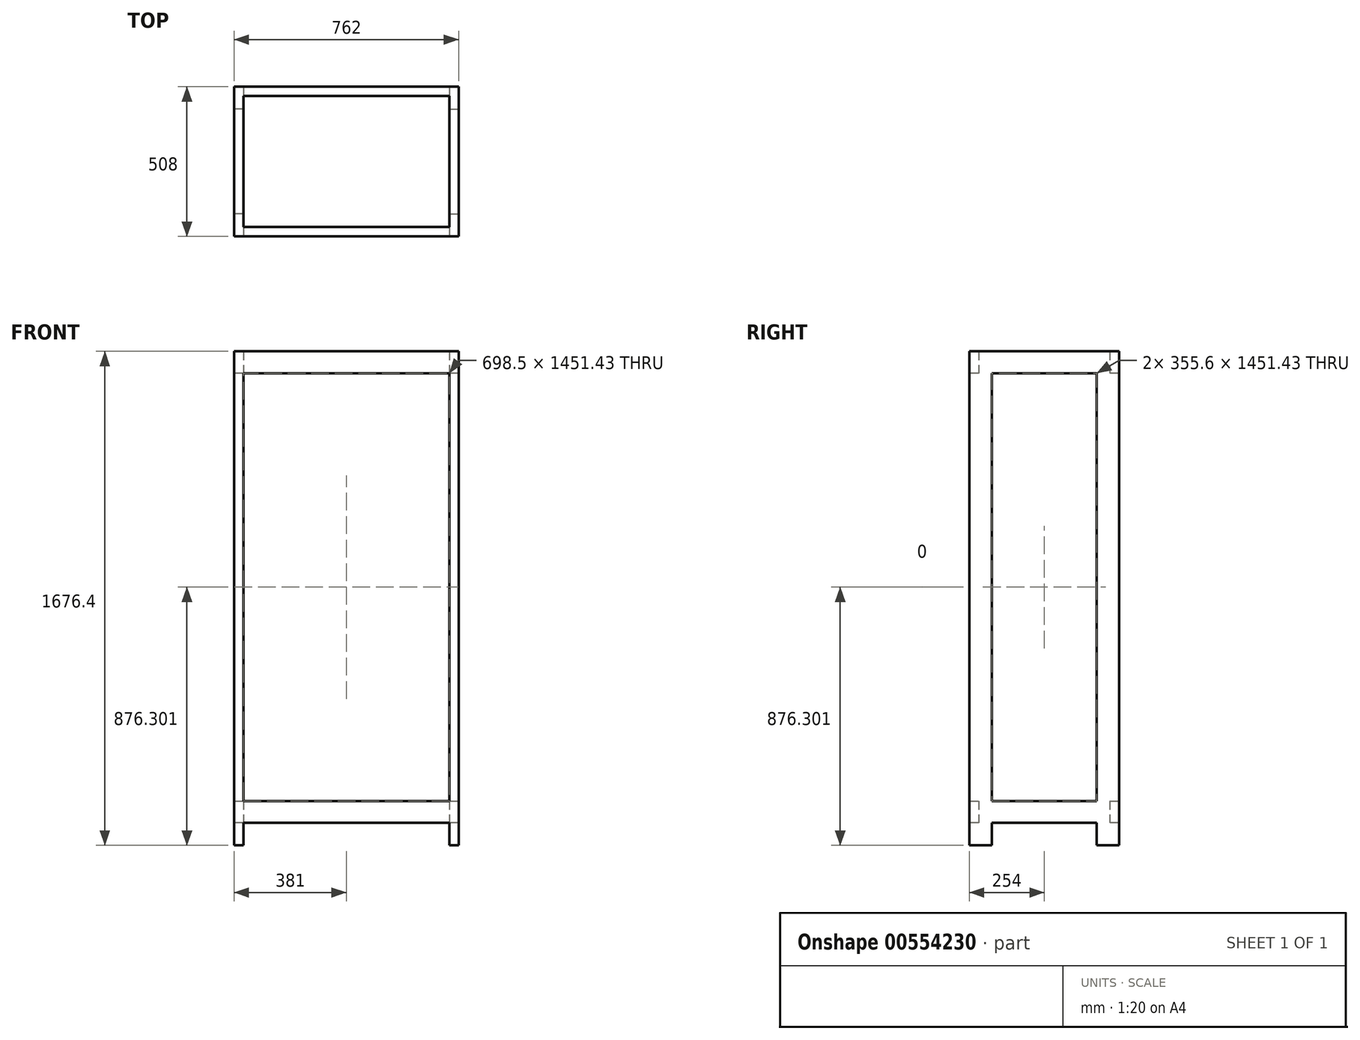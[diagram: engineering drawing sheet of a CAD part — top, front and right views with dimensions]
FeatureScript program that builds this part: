
annotation { "Feature Type Name" : "Feature", "Feature Type Description" : "" }
export const myFeature = defineFeature(function(context is Context, id is Id, definition is map)
    precondition{}
    {
        {
            var Q0;
            Q0=qCreatedBy(makeId("Front.planeOp"),FACE);
            var sketch = newSketch(context, id + "F0", { "sketchPlane" : qUnion([Q0])});
            skLineSegment(sketch, "E0.bottom", {"start": v(381, 1497.94) * mm, "end": v(349.25, 1497.94) * mm});
            skLineSegment(sketch, "E0.top", {"start": v(381, -178.46) * mm, "end": v(349.25, -178.46) * mm});
            skLineSegment(sketch, "E0.left", {"start": v(381, 1497.94) * mm, "end": v(381, -178.46) * mm});
            skLineSegment(sketch, "E0.right", {"start": v(349.25, 1497.94) * mm, "end": v(349.25, -178.46) * mm});
            skLineSegment(sketch, "E1", {"start": v(0, 72.38) * mm, "end": v(0, -157.13) * mm, "construction": true});
            skLineSegment(sketch, "E2.MirrorCS", {"start": v(-381, 1497.94) * mm, "end": v(-381, -178.46) * mm});
            skLineSegment(sketch, "E3.MirrorCS", {"start": v(-349.25, 1497.94) * mm, "end": v(-349.25, -178.46) * mm});
            skLineSegment(sketch, "E4.MirrorCS", {"start": v(-381, -178.46) * mm, "end": v(-349.25, -178.46) * mm});
            skLineSegment(sketch, "E5.MirrorCS", {"start": v(-381, 1497.94) * mm, "end": v(-349.25, 1497.94) * mm});
            skLineSegment(sketch, "E6", {"start": v(-349.25, 1497.94) * mm, "end": v(-349.25, 1423.55) * mm});
            skLineSegment(sketch, "E7", {"start": v(-349.25, 1423.55) * mm, "end": v(349.25, 1423.55) * mm});
            skLineSegment(sketch, "E8", {"start": v(349.25, 1423.55) * mm, "end": v(349.25, 1497.94) * mm});
            skLineSegment(sketch, "E9", {"start": v(-349.25, 1497.94) * mm, "end": v(349.25, 1497.94) * mm});
            skLineSegment(sketch, "E10", {"start": v(349.25, 697.84) * mm, "end": v(-349.25, 697.84) * mm, "construction": true});
            skLineSegment(sketch, "E11.MirrorCS", {"start": v(-349.25, -102.26) * mm, "end": v(349.25, -102.26) * mm});
            skLineSegment(sketch, "E12.MirrorCS", {"start": v(-349.25, -27.87) * mm, "end": v(349.25, -27.87) * mm});
            skLineSegment(sketch, "E13.MirrorCS", {"start": v(349.25, -27.87) * mm, "end": v(349.25, -102.26) * mm});
            skLineSegment(sketch, "E14.MirrorCS", {"start": v(-349.25, -102.26) * mm, "end": v(-349.25, -27.87) * mm});
            skLineSegment(sketch, "E15", {"start": v(-349.25, -65.07) * mm, "end": v(-365.12, -65.07) * mm});
            skLineSegment(sketch, "E16", {"start": v(-365.12, -65.07) * mm, "end": v(-365.13, 1460.75) * mm});
            skPoint(sketch, "E16.endSnap0", {"position": v(-349.25, 1460.75) * mm});
            skLineSegment(sketch, "E17", {"start": v(-365.13, 1460.75) * mm, "end": v(-349.25, 1460.75) * mm});
            skLineSegment(sketch, "E18", {"start": v(0, 1460.75) * mm, "end": v(-349.25, 1460.75) * mm});
            skLineSegment(sketch, "E19", {"start": v(0, -65.07) * mm, "end": v(-349.25, -65.07) * mm});
            skLineSegment(sketch, "E20.MirrorCS", {"start": v(0, -65.07) * mm, "end": v(349.25, -65.07) * mm});
            skLineSegment(sketch, "E21.MirrorCS", {"start": v(365.12, -65.07) * mm, "end": v(365.12, 1460.75) * mm});
            skLineSegment(sketch, "E22.MirrorCS", {"start": v(349.25, -65.07) * mm, "end": v(365.13, -65.07) * mm});
            skLineSegment(sketch, "E23.MirrorCS", {"start": v(365.12, 1460.75) * mm, "end": v(349.25, 1460.75) * mm});
            skLineSegment(sketch, "E24.MirrorCS", {"start": v(0, 1460.75) * mm, "end": v(349.25, 1460.75) * mm});
            skLineSegment(sketch, "E25", {"start": v(-349.25, 1423.55) * mm, "end": v(-381, 1423.55) * mm});
            skLineSegment(sketch, "E26", {"start": v(-349.25, -102.26) * mm, "end": v(-381, -102.26) * mm});
            skLineSegment(sketch, "E27", {"start": v(-381, -102.26) * mm, "end": v(-381, -27.87) * mm});
            skLineSegment(sketch, "E28", {"start": v(-381, -27.87) * mm, "end": v(-349.25, -27.87) * mm});
            skLineSegment(sketch, "E29.MirrorCS", {"start": v(349.25, -102.26) * mm, "end": v(381, -102.26) * mm});
            skLineSegment(sketch, "E30.MirrorCS", {"start": v(381, -27.87) * mm, "end": v(349.25, -27.87) * mm});
            skLineSegment(sketch, "E31.MirrorCS", {"start": v(381, -102.26) * mm, "end": v(381, -27.87) * mm});
            skLineSegment(sketch, "E32.MirrorCS", {"start": v(349.25, 1423.55) * mm, "end": v(381, 1423.55) * mm});
            skLineSegment(sketch, "E33.0", {"start": v(-349.25, -39.67) * mm, "end": v(-365.12, -39.67) * mm});
            skLineSegment(sketch, "E33.1", {"start": v(0, -39.67) * mm, "end": v(-349.25, -39.67) * mm});
            skLineSegment(sketch, "E33.2", {"start": v(0, -39.67) * mm, "end": v(349.25, -39.67) * mm});
            skLineSegment(sketch, "E33.3", {"start": v(349.25, -39.67) * mm, "end": v(365.13, -39.67) * mm});
            skLineSegment(sketch, "E34.0", {"start": v(365.12, 1435.35) * mm, "end": v(349.25, 1435.35) * mm});
            skLineSegment(sketch, "E34.1", {"start": v(0, 1435.35) * mm, "end": v(349.25, 1435.35) * mm});
            skLineSegment(sketch, "E34.2", {"start": v(0, 1435.35) * mm, "end": v(-349.25, 1435.35) * mm});
            skLineSegment(sketch, "E34.3", {"start": v(-365.13, 1435.35) * mm, "end": v(-349.25, 1435.35) * mm});
            skSolve(sketch);
        }
        {
            var Q0;
            {var subQ3=sQuery(id+"F0.wireOp",EDGE,"E23.MirrorCS");Q0=makeQuery(id+"F0.imprint","IMPRINT",FACE,{"disambiguationData":[TD([[makeQuery(id+"F0.imprint","IMPRINT",EDGE,{"derivedFrom":subQ3}),1.0]])]});}
            var Q1;
            {var subQ5=sQuery(id+"F0.wireOp",EDGE,"E0.bottom");Q1=makeQuery(id+"F0.imprint","IMPRINT",FACE,{"disambiguationData":[TD([[makeQuery(id+"F0.imprint","IMPRINT",EDGE,{"derivedFrom":subQ5}),1.0]])]});}
            var Q2;
            {var subQ0=sQuery(id+"F0.wireOp",EDGE,"E30.MirrorCS");var subQ5=sQuery(id+"F0.wireOp",EDGE,"E21.MirrorCS");var subQ6=makeQuery(id+"F0.imprint","INTERSECT",VERTEX,{"derivedFrom":[subQ5,subQ0]});Q2=makeQuery(id+"F0.imprint","IMPRINT",FACE,{"disambiguationData":[TD([[makeQuery(id+"F0.imprint","IMPRINT",EDGE,{"disambiguationData":[TD([[subQ6,-1.0]])],"derivedFrom":subQ5}),-1.0]])]});}
            var Q3;
            {var subQ3=sQuery(id+"F0.wireOp",EDGE,"E30.MirrorCS");var subQ5=sQuery(id+"F0.wireOp",EDGE,"E21.MirrorCS");var subQ6=makeQuery(id+"F0.imprint","INTERSECT",VERTEX,{"derivedFrom":[subQ5,subQ3]});Q3=makeQuery(id+"F0.imprint","IMPRINT",FACE,{"disambiguationData":[TD([[makeQuery(id+"F0.imprint","IMPRINT",EDGE,{"disambiguationData":[TD([[subQ6,-1.0]])],"derivedFrom":subQ5}),1.0]])]});}
            var Q4;
            {var subQ1=sQuery(id+"F0.wireOp",EDGE,"E22.MirrorCS");Q4=makeQuery(id+"F0.imprint","IMPRINT",FACE,{"disambiguationData":[TD([[makeQuery(id+"F0.imprint","IMPRINT",EDGE,{"derivedFrom":subQ1}),-1.0]])]});}
            var Q5;
            {var subQ3=sQuery(id+"F0.wireOp",EDGE,"E22.MirrorCS");Q5=makeQuery(id+"F0.imprint","IMPRINT",FACE,{"disambiguationData":[TD([[makeQuery(id+"F0.imprint","IMPRINT",EDGE,{"derivedFrom":subQ3}),1.0]])]});}
            var Q6;
            {var subQ0=sQuery(id+"F0.wireOp",EDGE,"E0.top");Q6=makeQuery(id+"F0.imprint","IMPRINT",FACE,{"disambiguationData":[TD([[makeQuery(id+"F0.imprint","IMPRINT",EDGE,{"derivedFrom":subQ0}),-1.0]])]});}
            var Q7;
            {var subQ0=sQuery(id+"F0.wireOp",EDGE,"E4.MirrorCS");Q7=makeQuery(id+"F0.imprint","IMPRINT",FACE,{"disambiguationData":[TD([[makeQuery(id+"F0.imprint","IMPRINT",EDGE,{"derivedFrom":subQ0}),1.0]])]});}
            var Q8;
            {var subQ2=sQuery(id+"F0.wireOp",EDGE,"E15");Q8=makeQuery(id+"F0.imprint","IMPRINT",FACE,{"disambiguationData":[TD([[makeQuery(id+"F0.imprint","IMPRINT",EDGE,{"derivedFrom":subQ2}),1.0]])]});}
            var Q9;
            {var subQ3=sQuery(id+"F0.wireOp",EDGE,"E15");Q9=makeQuery(id+"F0.imprint","IMPRINT",FACE,{"disambiguationData":[TD([[makeQuery(id+"F0.imprint","IMPRINT",EDGE,{"derivedFrom":subQ3}),-1.0]])]});}
            var Q10;
            {var subQ3=sQuery(id+"F0.wireOp",EDGE,"E28");var subQ5=sQuery(id+"F0.wireOp",EDGE,"E16");var subQ7=makeQuery(id+"F0.imprint","INTERSECT",VERTEX,{"derivedFrom":[subQ5,subQ3]});Q10=makeQuery(id+"F0.imprint","IMPRINT",FACE,{"disambiguationData":[TD([[makeQuery(id+"F0.imprint","IMPRINT",EDGE,{"disambiguationData":[TD([[subQ7,-1.0]])],"derivedFrom":subQ5}),-1.0]])]});}
            var Q11;
            {var subQ3=sQuery(id+"F0.wireOp",EDGE,"E28");var subQ5=sQuery(id+"F0.wireOp",EDGE,"E16");var subQ6=makeQuery(id+"F0.imprint","INTERSECT",VERTEX,{"derivedFrom":[subQ5,subQ3]});Q11=makeQuery(id+"F0.imprint","IMPRINT",FACE,{"disambiguationData":[TD([[makeQuery(id+"F0.imprint","IMPRINT",EDGE,{"disambiguationData":[TD([[subQ6,-1.0]])],"derivedFrom":subQ5}),1.0]])]});}
            var Q12;
            {var subQ3=sQuery(id+"F0.wireOp",EDGE,"E17");Q12=makeQuery(id+"F0.imprint","IMPRINT",FACE,{"disambiguationData":[TD([[makeQuery(id+"F0.imprint","IMPRINT",EDGE,{"derivedFrom":subQ3}),-1.0]])]});}
            var Q13;
            {var subQ4=sQuery(id+"F0.wireOp",EDGE,"E5.MirrorCS");Q13=makeQuery(id+"F0.imprint","IMPRINT",FACE,{"disambiguationData":[TD([[makeQuery(id+"F0.imprint","IMPRINT",EDGE,{"derivedFrom":subQ4}),-1.0]])]});}
            var Q14;
            {var subQ3=sQuery(id+"F0.wireOp",EDGE,"E34.0");Q14=makeQuery(id+"F0.imprint","IMPRINT",FACE,{"disambiguationData":[TD([[makeQuery(id+"F0.imprint","IMPRINT",EDGE,{"derivedFrom":subQ3}),1.0]])]});}
            var Q15;
            {var subQ3=sQuery(id+"F0.wireOp",EDGE,"E34.3");Q15=makeQuery(id+"F0.imprint","IMPRINT",FACE,{"disambiguationData":[TD([[makeQuery(id+"F0.imprint","IMPRINT",EDGE,{"derivedFrom":subQ3}),-1.0]])]});}
            var Q16;
            {var subQ3=sQuery(id+"F0.wireOp",EDGE,"E33.3");Q16=makeQuery(id+"F0.imprint","IMPRINT",FACE,{"disambiguationData":[TD([[makeQuery(id+"F0.imprint","IMPRINT",EDGE,{"derivedFrom":subQ3}),1.0]])]});}
            var Q17;
            {var subQ3=sQuery(id+"F0.wireOp",EDGE,"E33.0");Q17=makeQuery(id+"F0.imprint","IMPRINT",FACE,{"disambiguationData":[TD([[makeQuery(id+"F0.imprint","IMPRINT",EDGE,{"derivedFrom":subQ3}),-1.0]])]});}
            extrude(context, id + "F1", {"entities" : qUnion([Q0, Q1, Q2, Q3, Q4, Q5, Q6, Q7, Q8, Q9, Q10, Q11, Q12, Q13, Q14, Q15, Q16, Q17]), "depth" : 508 * mm, "offsetDistance" : 25.4 * mm});
        }
        {
            var Q0;
            Q0=makeQuery(id+"F1.opExtrude","CAP_FACE",FACE,{"disambiguationData":[OSD([sQuery(id+"F0.wireOp",EDGE,"E0.bottom"),sQuery(id+"F0.wireOp",EDGE,"E0.top"),sQuery(id+"F0.wireOp",EDGE,"E0.left"),sQuery(id+"F0.wireOp",EDGE,"E0.right"),sQuery(id+"F0.wireOp",EDGE,"E8"),sQuery(id+"F0.wireOp",EDGE,"E13.MirrorCS"),sQuery(id+"F0.wireOp",EDGE,"E31.MirrorCS")])],"isStart":true});
            var Q1;
            Q1=makeQuery(id+"F1.opExtrude","CAP_FACE",FACE,{"disambiguationData":[OSD([sQuery(id+"F0.wireOp",EDGE,"E2.MirrorCS"),sQuery(id+"F0.wireOp",EDGE,"E3.MirrorCS"),sQuery(id+"F0.wireOp",EDGE,"E4.MirrorCS"),sQuery(id+"F0.wireOp",EDGE,"E5.MirrorCS"),sQuery(id+"F0.wireOp",EDGE,"E6"),sQuery(id+"F0.wireOp",EDGE,"E14.MirrorCS"),sQuery(id+"F0.wireOp",EDGE,"E27")])],"isStart":true});
            extrude(context, id + "F2", {"entities" : qUnion([Q0, Q1]), "operationType" : NewBodyOperationType.REMOVE, "endBound" : BoundingType.UP_TO_NEXT, "oppositeDirection" : true, "depth" : 25.4 * mm, "hasOffset" : true, "offsetDistance" : 76.2 * mm, "hasSecondDirection" : true, "secondDirectionOppositeDirection" : false, "secondDirectionDepth" : -76.2 * mm});
        }
        {
            var Q0;
            {var subQ5=sQuery(id+"F0.wireOp",EDGE,"E0.bottom");Q0=makeQuery(id+"F0.imprint","IMPRINT",FACE,{"disambiguationData":[TD([[makeQuery(id+"F0.imprint","IMPRINT",EDGE,{"derivedFrom":subQ5}),1.0]])]});}
            var Q1;
            {var subQ4=sQuery(id+"F0.wireOp",EDGE,"E5.MirrorCS");Q1=makeQuery(id+"F0.imprint","IMPRINT",FACE,{"disambiguationData":[TD([[makeQuery(id+"F0.imprint","IMPRINT",EDGE,{"derivedFrom":subQ4}),-1.0]])]});}
            var Q2;
            {var subQ3=sQuery(id+"F0.wireOp",EDGE,"E17");Q2=makeQuery(id+"F0.imprint","IMPRINT",FACE,{"disambiguationData":[TD([[makeQuery(id+"F0.imprint","IMPRINT",EDGE,{"derivedFrom":subQ3}),-1.0]])]});}
            var Q3;
            {var subQ3=sQuery(id+"F0.wireOp",EDGE,"E22.MirrorCS");Q3=makeQuery(id+"F0.imprint","IMPRINT",FACE,{"disambiguationData":[TD([[makeQuery(id+"F0.imprint","IMPRINT",EDGE,{"derivedFrom":subQ3}),1.0]])]});}
            var Q4;
            {var subQ1=sQuery(id+"F0.wireOp",EDGE,"E22.MirrorCS");Q4=makeQuery(id+"F0.imprint","IMPRINT",FACE,{"disambiguationData":[TD([[makeQuery(id+"F0.imprint","IMPRINT",EDGE,{"derivedFrom":subQ1}),-1.0]])]});}
            var Q5;
            {var subQ3=sQuery(id+"F0.wireOp",EDGE,"E15");Q5=makeQuery(id+"F0.imprint","IMPRINT",FACE,{"disambiguationData":[TD([[makeQuery(id+"F0.imprint","IMPRINT",EDGE,{"derivedFrom":subQ3}),-1.0]])]});}
            var Q6;
            {var subQ2=sQuery(id+"F0.wireOp",EDGE,"E15");Q6=makeQuery(id+"F0.imprint","IMPRINT",FACE,{"disambiguationData":[TD([[makeQuery(id+"F0.imprint","IMPRINT",EDGE,{"derivedFrom":subQ2}),1.0]])]});}
            var Q7;
            {var subQ3=sQuery(id+"F0.wireOp",EDGE,"E34.0");Q7=makeQuery(id+"F0.imprint","IMPRINT",FACE,{"disambiguationData":[TD([[makeQuery(id+"F0.imprint","IMPRINT",EDGE,{"derivedFrom":subQ3}),1.0]])]});}
            var Q8;
            {var subQ0=sQuery(id+"F0.wireOp",EDGE,"E23.MirrorCS");Q8=makeQuery(id+"F0.imprint","IMPRINT",FACE,{"disambiguationData":[TD([[makeQuery(id+"F0.imprint","IMPRINT",EDGE,{"derivedFrom":subQ0}),1.0]])]});}
            var Q9;
            {var subQ3=sQuery(id+"F0.wireOp",EDGE,"E34.3");Q9=makeQuery(id+"F0.imprint","IMPRINT",FACE,{"disambiguationData":[TD([[makeQuery(id+"F0.imprint","IMPRINT",EDGE,{"derivedFrom":subQ3}),-1.0]])]});}
            var Q10;
            {var subQ3=sQuery(id+"F0.wireOp",EDGE,"E33.3");Q10=makeQuery(id+"F0.imprint","IMPRINT",FACE,{"disambiguationData":[TD([[makeQuery(id+"F0.imprint","IMPRINT",EDGE,{"derivedFrom":subQ3}),1.0]])]});}
            var Q11;
            {var subQ3=sQuery(id+"F0.wireOp",EDGE,"E33.0");Q11=makeQuery(id+"F0.imprint","IMPRINT",FACE,{"disambiguationData":[TD([[makeQuery(id+"F0.imprint","IMPRINT",EDGE,{"derivedFrom":subQ3}),-1.0]])]});}
            var Q12;
            Q12=makeQuery(id+"F2.boolean.opBoolean","COPY",FACE,{"derivedFrom":makeQuery(id+"F2.opExtrude","CAP_FACE",FACE,{"disambiguationData":[OSD([sQuery(id+"F0.wireOp",EDGE,"E0.bottom"),sQuery(id+"F0.wireOp",EDGE,"E0.top"),sQuery(id+"F0.wireOp",EDGE,"E0.left"),sQuery(id+"F0.wireOp",EDGE,"E0.right"),sQuery(id+"F0.wireOp",EDGE,"E8"),sQuery(id+"F0.wireOp",EDGE,"E13.MirrorCS"),sQuery(id+"F0.wireOp",EDGE,"E31.MirrorCS")])],"isStart":false})});
            extrude(context, id + "F3", {"entities" : qUnion([Q0, Q1, Q2, Q3, Q4, Q5, Q6, Q7, Q8, Q9, Q10, Q11]), "endBound" : BoundingType.UP_TO_SURFACE, "depth" : -76.2 * mm, "endBoundEntityFace" : qUnion([Q12]), "hasOffset" : true, "offsetDistance" : -76.2 * mm});
        }
        {
            var Q0;
            {var subQ1=sQuery(id+"F0.wireOp",EDGE,"E9");Q0=makeQuery(id+"F0.imprint","IMPRINT",FACE,{"disambiguationData":[TD([[makeQuery(id+"F0.imprint","IMPRINT",EDGE,{"derivedFrom":subQ1}),-1.0]])]});}
            var Q1;
            {var subQ1=sQuery(id+"F0.wireOp",EDGE,"E7");Q1=makeQuery(id+"F0.imprint","IMPRINT",FACE,{"disambiguationData":[TD([[makeQuery(id+"F0.imprint","IMPRINT",EDGE,{"derivedFrom":subQ1}),1.0]])]});}
            var Q2;
            {var subQ1=sQuery(id+"F0.wireOp",EDGE,"E12.MirrorCS");Q2=makeQuery(id+"F0.imprint","IMPRINT",FACE,{"disambiguationData":[TD([[makeQuery(id+"F0.imprint","IMPRINT",EDGE,{"derivedFrom":subQ1}),-1.0]])]});}
            var Q3;
            {var subQ2=sQuery(id+"F0.wireOp",EDGE,"E11.MirrorCS");Q3=makeQuery(id+"F0.imprint","IMPRINT",FACE,{"disambiguationData":[TD([[makeQuery(id+"F0.imprint","IMPRINT",EDGE,{"derivedFrom":subQ2}),1.0]])]});}
            var Q4;
            {var subQ1=sQuery(id+"F0.wireOp",EDGE,"E19");Q4=makeQuery(id+"F0.imprint","IMPRINT",FACE,{"disambiguationData":[TD([[makeQuery(id+"F0.imprint","IMPRINT",EDGE,{"derivedFrom":subQ1}),-1.0]])]});}
            var Q5;
            {var subQ1=sQuery(id+"F0.wireOp",EDGE,"E18");Q5=makeQuery(id+"F0.imprint","IMPRINT",FACE,{"disambiguationData":[TD([[makeQuery(id+"F0.imprint","IMPRINT",EDGE,{"derivedFrom":subQ1}),1.0]])]});}
            extrude(context, id + "F4", {"entities" : qUnion([Q0, Q1, Q2, Q3, Q4, Q5]), "operationType" : NewBodyOperationType.ADD, "depth" : 508 * mm, "offsetDistance" : 25.4 * mm});
        }
        {
            var Q0;
            {var subQ1=sQuery(id+"F0.wireOp",EDGE,"E7");Q0=makeQuery(id+"F0.imprint","IMPRINT",FACE,{"disambiguationData":[TD([[makeQuery(id+"F0.imprint","IMPRINT",EDGE,{"derivedFrom":subQ1}),1.0]])]});}
            var Q1;
            {var subQ1=sQuery(id+"F0.wireOp",EDGE,"E9");Q1=makeQuery(id+"F0.imprint","IMPRINT",FACE,{"disambiguationData":[TD([[makeQuery(id+"F0.imprint","IMPRINT",EDGE,{"derivedFrom":subQ1}),-1.0]])]});}
            var Q2;
            {var subQ1=sQuery(id+"F0.wireOp",EDGE,"E12.MirrorCS");Q2=makeQuery(id+"F0.imprint","IMPRINT",FACE,{"disambiguationData":[TD([[makeQuery(id+"F0.imprint","IMPRINT",EDGE,{"derivedFrom":subQ1}),-1.0]])]});}
            var Q3;
            {var subQ2=sQuery(id+"F0.wireOp",EDGE,"E11.MirrorCS");Q3=makeQuery(id+"F0.imprint","IMPRINT",FACE,{"disambiguationData":[TD([[makeQuery(id+"F0.imprint","IMPRINT",EDGE,{"derivedFrom":subQ2}),1.0]])]});}
            var Q4;
            {var subQ1=sQuery(id+"F0.wireOp",EDGE,"E18");Q4=makeQuery(id+"F0.imprint","IMPRINT",FACE,{"disambiguationData":[TD([[makeQuery(id+"F0.imprint","IMPRINT",EDGE,{"derivedFrom":subQ1}),1.0]])]});}
            var Q5;
            {var subQ1=sQuery(id+"F0.wireOp",EDGE,"E19");Q5=makeQuery(id+"F0.imprint","IMPRINT",FACE,{"disambiguationData":[TD([[makeQuery(id+"F0.imprint","IMPRINT",EDGE,{"derivedFrom":subQ1}),-1.0]])]});}
            extrude(context, id + "F5", {"entities" : qUnion([Q0, Q1, Q2, Q3, Q4, Q5]), "operationType" : NewBodyOperationType.REMOVE, "endBound" : BoundingType.UP_TO_NEXT, "depth" : 25.4 * mm, "hasOffset" : true, "offsetDistance" : 31.75 * mm, "hasSecondDirection" : true, "secondDirectionOppositeDirection" : true, "secondDirectionDepth" : -31.75 * mm});
        }
    });
